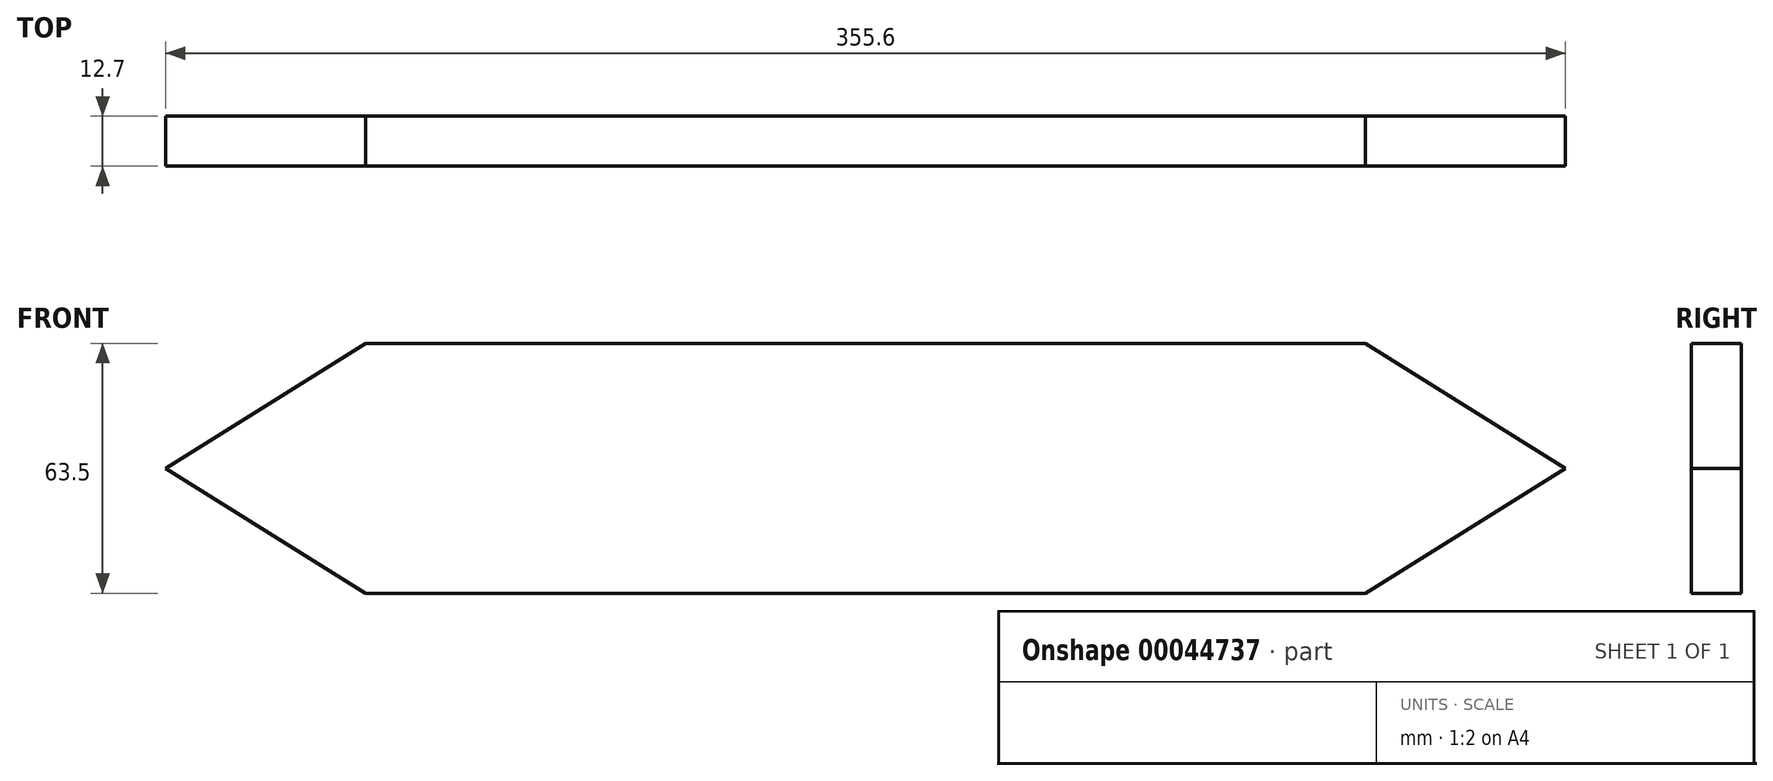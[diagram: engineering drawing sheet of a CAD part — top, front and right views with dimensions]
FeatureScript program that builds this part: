
annotation { "Feature Type Name" : "Feature", "Feature Type Description" : "" }
export const myFeature = defineFeature(function(context is Context, id is Id, definition is map)
    precondition{}
    {
        {
            var Q0;
            Q0=qCreatedBy(makeId("Front.planeOp"),FACE);
            var sketch = newSketch(context, id + "F0", { "sketchPlane" : qUnion([Q0])});
            skLineSegment(sketch, "E0.bottom", {"start": v(-162.63, -31.75) * mm, "end": v(91.37, -31.75) * mm});
            skLineSegment(sketch, "E0.top", {"start": v(-162.63, 31.75) * mm, "end": v(91.37, 31.75) * mm});
            skLineSegment(sketch, "E0.left", {"start": v(-162.63, -31.75) * mm, "end": v(-162.63, 31.75) * mm});
            skLineSegment(sketch, "E0.right", {"start": v(91.37, -31.75) * mm, "end": v(91.37, 31.75) * mm});
            skLineSegment(sketch, "E1", {"start": v(-162.63, 31.75) * mm, "end": v(-213.43, 0) * mm});
            skLineSegment(sketch, "E2", {"start": v(-213.43, 0) * mm, "end": v(-162.63, -31.75) * mm});
            skLineSegment(sketch, "E3", {"start": v(91.37, 31.75) * mm, "end": v(142.17, 0) * mm});
            skLineSegment(sketch, "E4", {"start": v(142.17, 0) * mm, "end": v(91.37, -31.75) * mm});
            skSolve(sketch);
        }
        {
            var Q0;
            Q0=qSketchRegion(id+"F0",true);
            extrude(context, id + "F1", {"entities" : qUnion([Q0]), "depth" : 12.7 * mm});
        }
    });
